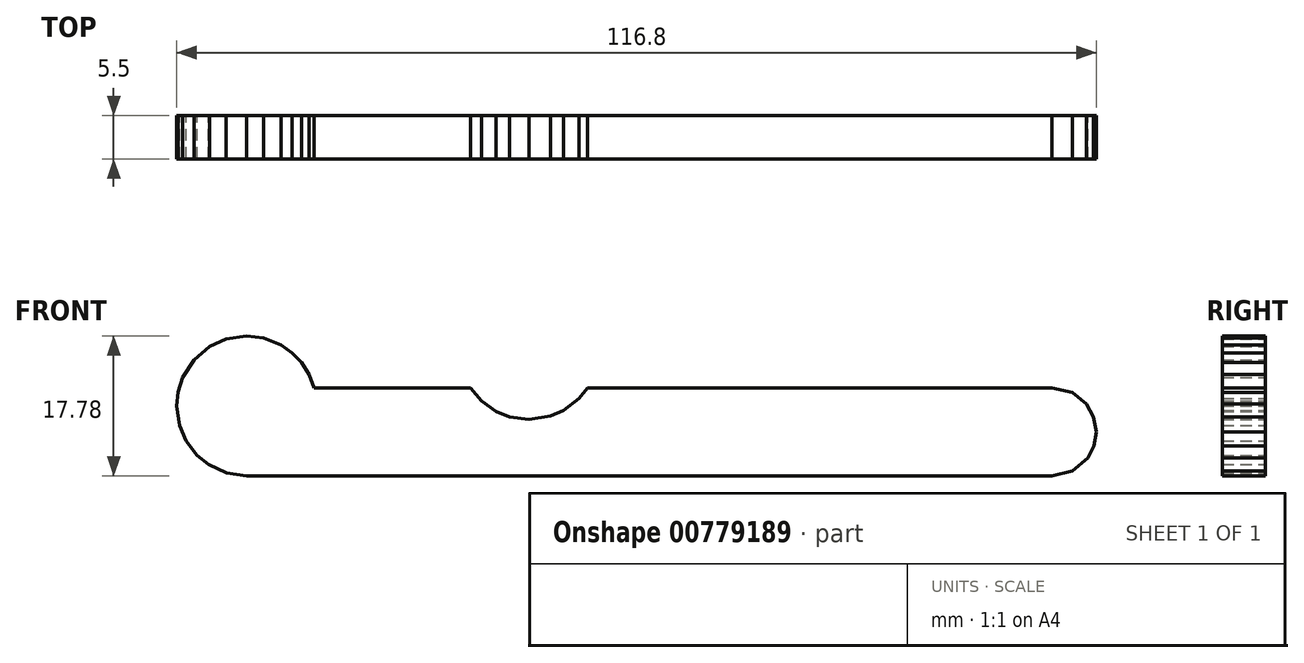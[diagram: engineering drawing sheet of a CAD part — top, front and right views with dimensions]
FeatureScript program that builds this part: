
annotation { "Feature Type Name" : "Feature", "Feature Type Description" : "" }
export const myFeature = defineFeature(function(context is Context, id is Id, definition is map)
    precondition{}
    {
        {
            var Q0;
            Q0=qCreatedBy(makeId("Front.planeOp"),FACE);
            var sketch = newSketch(context, id + "F0", { "sketchPlane" : qUnion([Q0])});
            skLineSegment(sketch, "E0", {"start": v(52.8, 2.31) * mm, "end": v(-6.22, 2.31) * mm});
            skLineSegment(sketch, "E1", {"start": v(-6.22, 2.31) * mm, "end": v(-7.31, 0.95) * mm});
            skLineSegment(sketch, "E2", {"start": v(-7.31, 0.95) * mm, "end": v(-9.28, -0.57) * mm});
            skLineSegment(sketch, "E3", {"start": v(-9.28, -0.57) * mm, "end": v(-10.91, -1.29) * mm});
            skLineSegment(sketch, "E4", {"start": v(-10.91, -1.29) * mm, "end": v(-13.66, -1.72) * mm});
            skLineSegment(sketch, "E5", {"start": v(-13.66, -1.72) * mm, "end": v(-16.11, -1.38) * mm});
            skLineSegment(sketch, "E6", {"start": v(-16.11, -1.38) * mm, "end": v(-17.83, -0.68) * mm});
            skLineSegment(sketch, "E7", {"start": v(-17.83, -0.68) * mm, "end": v(-19.66, 0.6) * mm});
            skLineSegment(sketch, "E8", {"start": v(-19.66, 0.6) * mm, "end": v(-21.1, 2.31) * mm});
            skLineSegment(sketch, "E9", {"start": v(-21.1, 2.31) * mm, "end": v(-40.93, 2.31) * mm});
            skLineSegment(sketch, "E10", {"start": v(-40.93, 2.31) * mm, "end": v(-41.58, 4.01) * mm});
            skLineSegment(sketch, "E11", {"start": v(-41.58, 4.01) * mm, "end": v(-42.57, 5.55) * mm});
            skLineSegment(sketch, "E12", {"start": v(-42.57, 5.55) * mm, "end": v(-43.74, 6.76) * mm});
            skLineSegment(sketch, "E13", {"start": v(-43.74, 6.76) * mm, "end": v(-45.12, 7.73) * mm});
            skLineSegment(sketch, "E14", {"start": v(-45.12, 7.73) * mm, "end": v(-47.37, 8.63) * mm});
            skLineSegment(sketch, "E15", {"start": v(-47.37, 8.63) * mm, "end": v(-49.5, 8.9) * mm});
            skLineSegment(sketch, "E16", {"start": v(-49.5, 8.9) * mm, "end": v(-52.15, 8.5) * mm});
            skLineSegment(sketch, "E17", {"start": v(-52.15, 8.5) * mm, "end": v(-54.24, 7.53) * mm});
            skLineSegment(sketch, "E18", {"start": v(-54.24, 7.53) * mm, "end": v(-56.22, 5.83) * mm});
            skLineSegment(sketch, "E19", {"start": v(-56.22, 5.83) * mm, "end": v(-57.63, 3.6) * mm});
            skLineSegment(sketch, "E20", {"start": v(-57.63, 3.6) * mm, "end": v(-58.22, 1.75) * mm});
            skLineSegment(sketch, "E21", {"start": v(-58.22, 1.75) * mm, "end": v(-58.4, 0) * mm});
            skLineSegment(sketch, "E22", {"start": v(-58.4, 0) * mm, "end": v(-58.05, -2.45) * mm});
            skLineSegment(sketch, "E23", {"start": v(-58.05, -2.45) * mm, "end": v(-57.2, -4.44) * mm});
            skLineSegment(sketch, "E24", {"start": v(-57.2, -4.44) * mm, "end": v(-55.82, -6.26) * mm});
            skLineSegment(sketch, "E25", {"start": v(-55.82, -6.26) * mm, "end": v(-54.37, -7.44) * mm});
            skLineSegment(sketch, "E26", {"start": v(-54.37, -7.44) * mm, "end": v(-52.09, -8.5) * mm});
            skLineSegment(sketch, "E27", {"start": v(-52.09, -8.5) * mm, "end": v(-49.5, -8.89) * mm});
            skLineSegment(sketch, "E28", {"start": v(-49.5, -8.89) * mm, "end": v(52.78, -8.89) * mm});
            skLineSegment(sketch, "E29", {"start": v(52.78, -8.89) * mm, "end": v(52.8, -8.9) * mm});
            skLineSegment(sketch, "E30", {"start": v(52.8, -8.9) * mm, "end": v(55.37, -8.27) * mm});
            skLineSegment(sketch, "E31", {"start": v(55.37, -8.27) * mm, "end": v(57.31, -6.6) * mm});
            skLineSegment(sketch, "E32", {"start": v(57.31, -6.6) * mm, "end": v(58.1, -5.08) * mm});
            skLineSegment(sketch, "E33", {"start": v(58.1, -5.08) * mm, "end": v(58.4, -3.29) * mm});
            skLineSegment(sketch, "E34", {"start": v(58.4, -3.29) * mm, "end": v(58.06, -1.38) * mm});
            skLineSegment(sketch, "E35", {"start": v(58.06, -1.38) * mm, "end": v(57.14, 0.24) * mm});
            skLineSegment(sketch, "E36", {"start": v(57.14, 0.24) * mm, "end": v(55.35, 1.7) * mm});
            skLineSegment(sketch, "E37", {"start": v(55.35, 1.7) * mm, "end": v(52.8, 2.31) * mm});
            skSolve(sketch);
        }
        {
            var Q0;
            Q0 = qSketchRegion(id + "F0", true);
            extrude(context, id + "F1", {"entities" : qUnion([Q0]), "depth" : 5.5 * mm, "offsetDistance" : 25.4 * mm});
        }
    });
